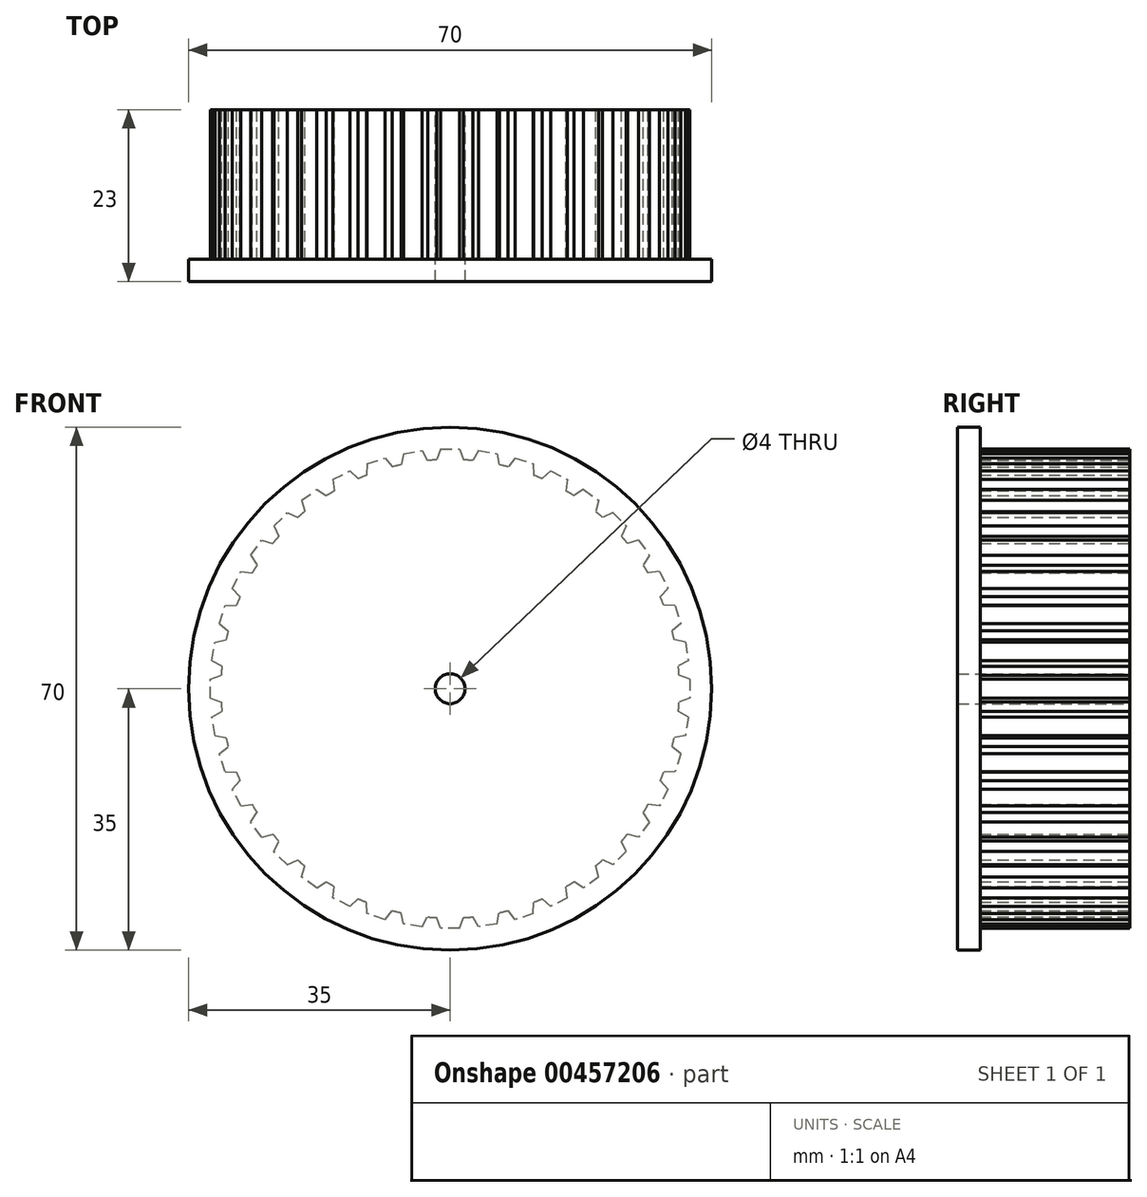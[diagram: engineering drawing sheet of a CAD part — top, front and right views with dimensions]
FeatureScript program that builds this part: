
annotation { "Feature Type Name" : "Feature", "Feature Type Description" : "" }
export const myFeature = defineFeature(function(context is Context, id is Id, definition is map)
    precondition{}
    {
        {
            var Q0;
            Q0=qCreatedBy(makeId("Front.planeOp"),FACE);
            var sketch = newSketch(context, id + "F0", { "sketchPlane" : qUnion([Q0])});
            skCircle(sketch, "E0", {"center": v(0, 0) * mm, "radius": 32.09 * mm, "construction": true});
            skLineSegment(sketch, "E1", {"start": v(0, 32.09) * mm, "end": v(0, 30.69) * mm, "construction": true});
            skCircle(sketch, "E2", {"center": v(0, 0) * mm, "radius": 30.69 * mm});
            skLineSegment(sketch, "E3", {"start": v(0, 0) * mm, "end": v(-1.26, 32.06) * mm, "construction": true});
            skLineSegment(sketch, "E4", {"start": v(0, 0) * mm, "end": v(-2.52, 31.99) * mm, "construction": true});
            skLineSegment(sketch, "E5.MirrorCS", {"start": v(0, 0) * mm, "end": v(1.26, 32.06) * mm, "construction": true});
            skLineSegment(sketch, "E6.MirrorCS", {"start": v(0, 0) * mm, "end": v(2.52, 31.99) * mm, "construction": true});
            skLineSegment(sketch, "E7", {"start": v(-1.26, 32.06) * mm, "end": v(1.26, 32.06) * mm});
            skLineSegment(sketch, "E8", {"start": v(-1.26, 32.06) * mm, "end": v(-1.8, 30.63) * mm});
            skLineSegment(sketch, "E9.MirrorCS", {"start": v(1.26, 32.06) * mm, "end": v(1.8, 30.63) * mm});
            skLineSegment(sketch, "E10.1.0", {"start": v(-6.26, 31.47) * mm, "end": v(-6.56, 29.97) * mm});
            skLineSegment(sketch, "E10.1.1", {"start": v(-6.26, 31.47) * mm, "end": v(-3.77, 31.86) * mm});
            skLineSegment(sketch, "E10.1.2", {"start": v(-3.77, 31.86) * mm, "end": v(-3.02, 30.54) * mm});
            skLineSegment(sketch, "E10.2.0", {"start": v(-11.1, 30.1) * mm, "end": v(-11.17, 28.58) * mm});
            skLineSegment(sketch, "E10.2.1", {"start": v(-11.1, 30.1) * mm, "end": v(-8.7, 30.88) * mm});
            skLineSegment(sketch, "E10.2.2", {"start": v(-8.7, 30.88) * mm, "end": v(-7.76, 29.69) * mm});
            skLineSegment(sketch, "E10.3.0", {"start": v(-15.68, 28) * mm, "end": v(-15.5, 26.48) * mm});
            skLineSegment(sketch, "E10.3.1", {"start": v(-15.68, 28) * mm, "end": v(-13.43, 29.14) * mm});
            skLineSegment(sketch, "E10.3.2", {"start": v(-13.43, 29.14) * mm, "end": v(-12.3, 28.1) * mm});
            skLineSegment(sketch, "E10.4.0", {"start": v(-19.86, 25.2) * mm, "end": v(-19.46, 23.73) * mm});
            skLineSegment(sketch, "E10.4.1", {"start": v(-19.86, 25.2) * mm, "end": v(-17.83, 26.68) * mm});
            skLineSegment(sketch, "E10.4.2", {"start": v(-17.83, 26.68) * mm, "end": v(-16.55, 25.84) * mm});
            skLineSegment(sketch, "E10.5.0", {"start": v(-23.56, 21.78) * mm, "end": v(-22.93, 20.4) * mm});
            skLineSegment(sketch, "E10.5.1", {"start": v(-23.56, 21.78) * mm, "end": v(-21.78, 23.56) * mm});
            skLineSegment(sketch, "E10.5.2", {"start": v(-21.78, 23.56) * mm, "end": v(-20.4, 22.93) * mm});
            skLineSegment(sketch, "E10.6.0", {"start": v(-26.68, 17.83) * mm, "end": v(-25.84, 16.55) * mm});
            skLineSegment(sketch, "E10.6.1", {"start": v(-26.68, 17.83) * mm, "end": v(-25.2, 19.86) * mm});
            skLineSegment(sketch, "E10.6.2", {"start": v(-25.2, 19.86) * mm, "end": v(-23.73, 19.46) * mm});
            skLineSegment(sketch, "E10.7.0", {"start": v(-29.14, 13.43) * mm, "end": v(-28.1, 12.3) * mm});
            skLineSegment(sketch, "E10.7.1", {"start": v(-29.14, 13.43) * mm, "end": v(-28, 15.68) * mm});
            skLineSegment(sketch, "E10.7.2", {"start": v(-28, 15.68) * mm, "end": v(-26.48, 15.5) * mm});
            skLineSegment(sketch, "E10.8.0", {"start": v(-30.88, 8.7) * mm, "end": v(-29.69, 7.76) * mm});
            skLineSegment(sketch, "E10.8.1", {"start": v(-30.88, 8.7) * mm, "end": v(-30.1, 11.1) * mm});
            skLineSegment(sketch, "E10.8.2", {"start": v(-30.1, 11.1) * mm, "end": v(-28.58, 11.17) * mm});
            skLineSegment(sketch, "E10.9.0", {"start": v(-31.86, 3.77) * mm, "end": v(-30.54, 3.02) * mm});
            skLineSegment(sketch, "E10.9.1", {"start": v(-31.86, 3.77) * mm, "end": v(-31.47, 6.26) * mm});
            skLineSegment(sketch, "E10.9.2", {"start": v(-31.47, 6.26) * mm, "end": v(-29.97, 6.56) * mm});
            skLineSegment(sketch, "E11", {"start": v(0, 0) * mm, "end": v(0, 32.09) * mm, "construction": true});
            skLineSegment(sketch, "E12.2.10.0", {"start": v(-32.06, -1.26) * mm, "end": v(-30.63, -1.8) * mm});
            skLineSegment(sketch, "E12.3.10.0", {"start": v(-32.06, -1.26) * mm, "end": v(-32.06, 1.26) * mm});
            skLineSegment(sketch, "E12.6.10.0", {"start": v(-32.06, 1.26) * mm, "end": v(-30.63, 1.8) * mm});
            skLineSegment(sketch, "E12.2.11.0", {"start": v(-31.47, -6.26) * mm, "end": v(-29.97, -6.56) * mm});
            skLineSegment(sketch, "E12.3.11.0", {"start": v(-31.47, -6.26) * mm, "end": v(-31.86, -3.77) * mm});
            skLineSegment(sketch, "E12.6.11.0", {"start": v(-31.86, -3.77) * mm, "end": v(-30.54, -3.02) * mm});
            skLineSegment(sketch, "E12.2.12.0", {"start": v(-30.1, -11.1) * mm, "end": v(-28.58, -11.17) * mm});
            skLineSegment(sketch, "E12.3.12.0", {"start": v(-30.1, -11.1) * mm, "end": v(-30.88, -8.7) * mm});
            skLineSegment(sketch, "E12.6.12.0", {"start": v(-30.88, -8.7) * mm, "end": v(-29.69, -7.76) * mm});
            skLineSegment(sketch, "E12.2.13.0", {"start": v(-28, -15.68) * mm, "end": v(-26.48, -15.5) * mm});
            skLineSegment(sketch, "E12.3.13.0", {"start": v(-28, -15.68) * mm, "end": v(-29.14, -13.43) * mm});
            skLineSegment(sketch, "E12.6.13.0", {"start": v(-29.14, -13.43) * mm, "end": v(-28.1, -12.3) * mm});
            skLineSegment(sketch, "E12.2.14.0", {"start": v(-25.2, -19.86) * mm, "end": v(-23.73, -19.46) * mm});
            skLineSegment(sketch, "E12.3.14.0", {"start": v(-25.2, -19.86) * mm, "end": v(-26.68, -17.83) * mm});
            skLineSegment(sketch, "E12.6.14.0", {"start": v(-26.68, -17.83) * mm, "end": v(-25.84, -16.55) * mm});
            skLineSegment(sketch, "E12.2.15.0", {"start": v(-21.78, -23.56) * mm, "end": v(-20.4, -22.93) * mm});
            skLineSegment(sketch, "E12.3.15.0", {"start": v(-21.78, -23.56) * mm, "end": v(-23.56, -21.78) * mm});
            skLineSegment(sketch, "E12.6.15.0", {"start": v(-23.56, -21.78) * mm, "end": v(-22.93, -20.4) * mm});
            skLineSegment(sketch, "E12.2.16.0", {"start": v(-17.83, -26.68) * mm, "end": v(-16.55, -25.84) * mm});
            skLineSegment(sketch, "E12.3.16.0", {"start": v(-17.83, -26.68) * mm, "end": v(-19.86, -25.2) * mm});
            skLineSegment(sketch, "E12.6.16.0", {"start": v(-19.86, -25.2) * mm, "end": v(-19.46, -23.73) * mm});
            skLineSegment(sketch, "E12.2.17.0", {"start": v(-13.43, -29.14) * mm, "end": v(-12.3, -28.1) * mm});
            skLineSegment(sketch, "E12.3.17.0", {"start": v(-13.43, -29.14) * mm, "end": v(-15.68, -28) * mm});
            skLineSegment(sketch, "E12.6.17.0", {"start": v(-15.68, -28) * mm, "end": v(-15.5, -26.48) * mm});
            skLineSegment(sketch, "E12.2.18.0", {"start": v(-8.7, -30.88) * mm, "end": v(-7.76, -29.69) * mm});
            skLineSegment(sketch, "E12.3.18.0", {"start": v(-8.7, -30.88) * mm, "end": v(-11.1, -30.1) * mm});
            skLineSegment(sketch, "E12.6.18.0", {"start": v(-11.1, -30.1) * mm, "end": v(-11.17, -28.58) * mm});
            skLineSegment(sketch, "E12.2.19.0", {"start": v(-3.77, -31.86) * mm, "end": v(-3.02, -30.54) * mm});
            skLineSegment(sketch, "E12.3.19.0", {"start": v(-3.77, -31.86) * mm, "end": v(-6.26, -31.47) * mm});
            skLineSegment(sketch, "E12.6.19.0", {"start": v(-6.26, -31.47) * mm, "end": v(-6.56, -29.97) * mm});
            skLineSegment(sketch, "E12.2.20.0", {"start": v(1.26, -32.06) * mm, "end": v(1.8, -30.63) * mm});
            skLineSegment(sketch, "E12.3.20.0", {"start": v(1.26, -32.06) * mm, "end": v(-1.26, -32.06) * mm});
            skLineSegment(sketch, "E12.6.20.0", {"start": v(-1.26, -32.06) * mm, "end": v(-1.8, -30.63) * mm});
            skLineSegment(sketch, "E12.2.21.0", {"start": v(6.26, -31.47) * mm, "end": v(6.56, -29.97) * mm});
            skLineSegment(sketch, "E12.3.21.0", {"start": v(6.26, -31.47) * mm, "end": v(3.77, -31.86) * mm});
            skLineSegment(sketch, "E12.6.21.0", {"start": v(3.77, -31.86) * mm, "end": v(3.02, -30.54) * mm});
            skLineSegment(sketch, "E12.2.22.0", {"start": v(11.1, -30.1) * mm, "end": v(11.17, -28.58) * mm});
            skLineSegment(sketch, "E12.3.22.0", {"start": v(11.1, -30.1) * mm, "end": v(8.7, -30.88) * mm});
            skLineSegment(sketch, "E12.6.22.0", {"start": v(8.7, -30.88) * mm, "end": v(7.76, -29.69) * mm});
            skLineSegment(sketch, "E12.2.23.0", {"start": v(15.68, -28) * mm, "end": v(15.5, -26.48) * mm});
            skLineSegment(sketch, "E12.3.23.0", {"start": v(15.68, -28) * mm, "end": v(13.43, -29.14) * mm});
            skLineSegment(sketch, "E12.6.23.0", {"start": v(13.43, -29.14) * mm, "end": v(12.3, -28.1) * mm});
            skLineSegment(sketch, "E12.2.24.0", {"start": v(19.86, -25.2) * mm, "end": v(19.46, -23.73) * mm});
            skLineSegment(sketch, "E12.3.24.0", {"start": v(19.86, -25.2) * mm, "end": v(17.83, -26.68) * mm});
            skLineSegment(sketch, "E12.6.24.0", {"start": v(17.83, -26.68) * mm, "end": v(16.55, -25.84) * mm});
            skLineSegment(sketch, "E12.2.25.0", {"start": v(23.56, -21.78) * mm, "end": v(22.93, -20.4) * mm});
            skLineSegment(sketch, "E12.3.25.0", {"start": v(23.56, -21.78) * mm, "end": v(21.78, -23.56) * mm});
            skLineSegment(sketch, "E12.6.25.0", {"start": v(21.78, -23.56) * mm, "end": v(20.4, -22.93) * mm});
            skLineSegment(sketch, "E12.2.26.0", {"start": v(26.68, -17.83) * mm, "end": v(25.84, -16.55) * mm});
            skLineSegment(sketch, "E12.3.26.0", {"start": v(26.68, -17.83) * mm, "end": v(25.2, -19.86) * mm});
            skLineSegment(sketch, "E12.6.26.0", {"start": v(25.2, -19.86) * mm, "end": v(23.73, -19.46) * mm});
            skLineSegment(sketch, "E12.2.27.0", {"start": v(29.14, -13.43) * mm, "end": v(28.1, -12.3) * mm});
            skLineSegment(sketch, "E12.3.27.0", {"start": v(29.14, -13.43) * mm, "end": v(28, -15.68) * mm});
            skLineSegment(sketch, "E12.6.27.0", {"start": v(28, -15.68) * mm, "end": v(26.48, -15.5) * mm});
            skLineSegment(sketch, "E12.2.28.0", {"start": v(30.88, -8.7) * mm, "end": v(29.69, -7.76) * mm});
            skLineSegment(sketch, "E12.3.28.0", {"start": v(30.88, -8.7) * mm, "end": v(30.1, -11.1) * mm});
            skLineSegment(sketch, "E12.6.28.0", {"start": v(30.1, -11.1) * mm, "end": v(28.58, -11.17) * mm});
            skLineSegment(sketch, "E12.2.29.0", {"start": v(31.86, -3.77) * mm, "end": v(30.54, -3.02) * mm});
            skLineSegment(sketch, "E12.3.29.0", {"start": v(31.86, -3.77) * mm, "end": v(31.47, -6.26) * mm});
            skLineSegment(sketch, "E12.6.29.0", {"start": v(31.47, -6.26) * mm, "end": v(29.97, -6.56) * mm});
            skLineSegment(sketch, "E12.2.30.0", {"start": v(32.06, 1.26) * mm, "end": v(30.63, 1.8) * mm});
            skLineSegment(sketch, "E12.3.30.0", {"start": v(32.06, 1.26) * mm, "end": v(32.06, -1.26) * mm});
            skLineSegment(sketch, "E12.6.30.0", {"start": v(32.06, -1.26) * mm, "end": v(30.63, -1.8) * mm});
            skLineSegment(sketch, "E12.2.31.0", {"start": v(31.47, 6.26) * mm, "end": v(29.97, 6.56) * mm});
            skLineSegment(sketch, "E12.3.31.0", {"start": v(31.47, 6.26) * mm, "end": v(31.86, 3.77) * mm});
            skLineSegment(sketch, "E12.6.31.0", {"start": v(31.86, 3.77) * mm, "end": v(30.54, 3.02) * mm});
            skLineSegment(sketch, "E12.2.32.0", {"start": v(30.1, 11.1) * mm, "end": v(28.58, 11.17) * mm});
            skLineSegment(sketch, "E12.3.32.0", {"start": v(30.1, 11.1) * mm, "end": v(30.88, 8.7) * mm});
            skLineSegment(sketch, "E12.6.32.0", {"start": v(30.88, 8.7) * mm, "end": v(29.69, 7.76) * mm});
            skLineSegment(sketch, "E12.2.33.0", {"start": v(28, 15.68) * mm, "end": v(26.48, 15.5) * mm});
            skLineSegment(sketch, "E12.3.33.0", {"start": v(28, 15.68) * mm, "end": v(29.14, 13.43) * mm});
            skLineSegment(sketch, "E12.6.33.0", {"start": v(29.14, 13.43) * mm, "end": v(28.1, 12.3) * mm});
            skLineSegment(sketch, "E12.2.34.0", {"start": v(25.2, 19.86) * mm, "end": v(23.73, 19.46) * mm});
            skLineSegment(sketch, "E12.3.34.0", {"start": v(25.2, 19.86) * mm, "end": v(26.68, 17.83) * mm});
            skLineSegment(sketch, "E12.6.34.0", {"start": v(26.68, 17.83) * mm, "end": v(25.84, 16.55) * mm});
            skLineSegment(sketch, "E12.2.35.0", {"start": v(21.78, 23.56) * mm, "end": v(20.4, 22.93) * mm});
            skLineSegment(sketch, "E12.3.35.0", {"start": v(21.78, 23.56) * mm, "end": v(23.56, 21.78) * mm});
            skLineSegment(sketch, "E12.6.35.0", {"start": v(23.56, 21.78) * mm, "end": v(22.93, 20.4) * mm});
            skLineSegment(sketch, "E12.2.36.0", {"start": v(17.83, 26.68) * mm, "end": v(16.55, 25.84) * mm});
            skLineSegment(sketch, "E12.3.36.0", {"start": v(17.83, 26.68) * mm, "end": v(19.86, 25.2) * mm});
            skLineSegment(sketch, "E12.6.36.0", {"start": v(19.86, 25.2) * mm, "end": v(19.46, 23.73) * mm});
            skLineSegment(sketch, "E12.2.37.0", {"start": v(13.43, 29.14) * mm, "end": v(12.3, 28.1) * mm});
            skLineSegment(sketch, "E12.3.37.0", {"start": v(13.43, 29.14) * mm, "end": v(15.68, 28) * mm});
            skLineSegment(sketch, "E12.6.37.0", {"start": v(15.68, 28) * mm, "end": v(15.5, 26.48) * mm});
            skLineSegment(sketch, "E12.2.38.0", {"start": v(8.7, 30.88) * mm, "end": v(7.76, 29.69) * mm});
            skLineSegment(sketch, "E12.3.38.0", {"start": v(8.7, 30.88) * mm, "end": v(11.1, 30.1) * mm});
            skLineSegment(sketch, "E12.6.38.0", {"start": v(11.1, 30.1) * mm, "end": v(11.17, 28.58) * mm});
            skLineSegment(sketch, "E12.2.39.0", {"start": v(3.77, 31.86) * mm, "end": v(3.02, 30.54) * mm});
            skLineSegment(sketch, "E12.3.39.0", {"start": v(3.77, 31.86) * mm, "end": v(6.26, 31.47) * mm});
            skLineSegment(sketch, "E12.6.39.0", {"start": v(6.26, 31.47) * mm, "end": v(6.56, 29.97) * mm});
            skCircle(sketch, "E13", {"center": v(0, 0) * mm, "radius": 2 * mm});
            skSolve(sketch);
        }
        {
            var Q0;
            Q0=qSketchRegion(id+"F0",true);
            extrude(context, id + "F1", {"entities" : qUnion([Q0]), "depth" : 20 * mm, "offsetDistance" : 25 * mm});
        }
        {
            var Q0;
            Q0=makeQuery(id+"F1.opExtrude","CAP_FACE",FACE,{"disambiguationData":[OSD([sQuery(id+"F0.wireOp",EDGE,"E2"),sQuery(id+"F0.wireOp",EDGE,"E7"),sQuery(id+"F0.wireOp",EDGE,"E8"),sQuery(id+"F0.wireOp",EDGE,"E9.MirrorCS"),sQuery(id+"F0.wireOp",EDGE,"E10.1.0"),sQuery(id+"F0.wireOp",EDGE,"E10.1.1"),sQuery(id+"F0.wireOp",EDGE,"E10.1.2"),sQuery(id+"F0.wireOp",EDGE,"E10.2.0"),sQuery(id+"F0.wireOp",EDGE,"E10.2.1"),sQuery(id+"F0.wireOp",EDGE,"E10.2.2"),sQuery(id+"F0.wireOp",EDGE,"E10.3.0"),sQuery(id+"F0.wireOp",EDGE,"E10.3.1"),sQuery(id+"F0.wireOp",EDGE,"E10.3.2"),sQuery(id+"F0.wireOp",EDGE,"E10.4.0"),sQuery(id+"F0.wireOp",EDGE,"E10.4.1"),sQuery(id+"F0.wireOp",EDGE,"E10.4.2"),sQuery(id+"F0.wireOp",EDGE,"E10.5.0"),sQuery(id+"F0.wireOp",EDGE,"E10.5.1"),sQuery(id+"F0.wireOp",EDGE,"E10.5.2"),sQuery(id+"F0.wireOp",EDGE,"E10.6.0"),sQuery(id+"F0.wireOp",EDGE,"E10.6.1"),sQuery(id+"F0.wireOp",EDGE,"E10.6.2"),sQuery(id+"F0.wireOp",EDGE,"E10.7.0"),sQuery(id+"F0.wireOp",EDGE,"E10.7.1"),sQuery(id+"F0.wireOp",EDGE,"E10.7.2"),sQuery(id+"F0.wireOp",EDGE,"E10.8.0"),sQuery(id+"F0.wireOp",EDGE,"E10.8.1"),sQuery(id+"F0.wireOp",EDGE,"E10.8.2"),sQuery(id+"F0.wireOp",EDGE,"E10.9.0"),sQuery(id+"F0.wireOp",EDGE,"E10.9.1"),sQuery(id+"F0.wireOp",EDGE,"E10.9.2"),sQuery(id+"F0.wireOp",EDGE,"E12.2.10.0"),sQuery(id+"F0.wireOp",EDGE,"E12.3.10.0"),sQuery(id+"F0.wireOp",EDGE,"E12.6.10.0"),sQuery(id+"F0.wireOp",EDGE,"E12.2.11.0"),sQuery(id+"F0.wireOp",EDGE,"E12.3.11.0"),sQuery(id+"F0.wireOp",EDGE,"E12.6.11.0"),sQuery(id+"F0.wireOp",EDGE,"E12.2.12.0"),sQuery(id+"F0.wireOp",EDGE,"E12.3.12.0"),sQuery(id+"F0.wireOp",EDGE,"E12.6.12.0"),sQuery(id+"F0.wireOp",EDGE,"E12.2.13.0"),sQuery(id+"F0.wireOp",EDGE,"E12.3.13.0"),sQuery(id+"F0.wireOp",EDGE,"E12.6.13.0"),sQuery(id+"F0.wireOp",EDGE,"E12.2.14.0"),sQuery(id+"F0.wireOp",EDGE,"E12.3.14.0"),sQuery(id+"F0.wireOp",EDGE,"E12.6.14.0"),sQuery(id+"F0.wireOp",EDGE,"E12.2.15.0"),sQuery(id+"F0.wireOp",EDGE,"E12.3.15.0"),sQuery(id+"F0.wireOp",EDGE,"E12.6.15.0"),sQuery(id+"F0.wireOp",EDGE,"E12.2.16.0"),sQuery(id+"F0.wireOp",EDGE,"E12.3.16.0"),sQuery(id+"F0.wireOp",EDGE,"E12.6.16.0"),sQuery(id+"F0.wireOp",EDGE,"E12.2.17.0"),sQuery(id+"F0.wireOp",EDGE,"E12.3.17.0"),sQuery(id+"F0.wireOp",EDGE,"E12.6.17.0"),sQuery(id+"F0.wireOp",EDGE,"E12.2.18.0"),sQuery(id+"F0.wireOp",EDGE,"E12.3.18.0"),sQuery(id+"F0.wireOp",EDGE,"E12.6.18.0"),sQuery(id+"F0.wireOp",EDGE,"E12.2.19.0"),sQuery(id+"F0.wireOp",EDGE,"E12.3.19.0"),sQuery(id+"F0.wireOp",EDGE,"E12.6.19.0"),sQuery(id+"F0.wireOp",EDGE,"E12.2.20.0"),sQuery(id+"F0.wireOp",EDGE,"E12.3.20.0"),sQuery(id+"F0.wireOp",EDGE,"E12.6.20.0"),sQuery(id+"F0.wireOp",EDGE,"E12.2.21.0"),sQuery(id+"F0.wireOp",EDGE,"E12.3.21.0"),sQuery(id+"F0.wireOp",EDGE,"E12.6.21.0"),sQuery(id+"F0.wireOp",EDGE,"E12.2.22.0"),sQuery(id+"F0.wireOp",EDGE,"E12.3.22.0"),sQuery(id+"F0.wireOp",EDGE,"E12.6.22.0"),sQuery(id+"F0.wireOp",EDGE,"E12.2.23.0"),sQuery(id+"F0.wireOp",EDGE,"E12.3.23.0"),sQuery(id+"F0.wireOp",EDGE,"E12.6.23.0"),sQuery(id+"F0.wireOp",EDGE,"E12.2.24.0"),sQuery(id+"F0.wireOp",EDGE,"E12.3.24.0"),sQuery(id+"F0.wireOp",EDGE,"E12.6.24.0"),sQuery(id+"F0.wireOp",EDGE,"E12.2.25.0"),sQuery(id+"F0.wireOp",EDGE,"E12.3.25.0"),sQuery(id+"F0.wireOp",EDGE,"E12.6.25.0"),sQuery(id+"F0.wireOp",EDGE,"E12.2.26.0"),sQuery(id+"F0.wireOp",EDGE,"E12.3.26.0"),sQuery(id+"F0.wireOp",EDGE,"E12.6.26.0"),sQuery(id+"F0.wireOp",EDGE,"E12.2.27.0"),sQuery(id+"F0.wireOp",EDGE,"E12.3.27.0"),sQuery(id+"F0.wireOp",EDGE,"E12.6.27.0"),sQuery(id+"F0.wireOp",EDGE,"E12.2.28.0"),sQuery(id+"F0.wireOp",EDGE,"E12.3.28.0"),sQuery(id+"F0.wireOp",EDGE,"E12.6.28.0"),sQuery(id+"F0.wireOp",EDGE,"E12.2.29.0"),sQuery(id+"F0.wireOp",EDGE,"E12.3.29.0"),sQuery(id+"F0.wireOp",EDGE,"E12.6.29.0"),sQuery(id+"F0.wireOp",EDGE,"E12.2.30.0"),sQuery(id+"F0.wireOp",EDGE,"E12.3.30.0"),sQuery(id+"F0.wireOp",EDGE,"E12.6.30.0"),sQuery(id+"F0.wireOp",EDGE,"E12.2.31.0"),sQuery(id+"F0.wireOp",EDGE,"E12.3.31.0"),sQuery(id+"F0.wireOp",EDGE,"E12.6.31.0"),sQuery(id+"F0.wireOp",EDGE,"E12.2.32.0"),sQuery(id+"F0.wireOp",EDGE,"E12.3.32.0"),sQuery(id+"F0.wireOp",EDGE,"E12.6.32.0"),sQuery(id+"F0.wireOp",EDGE,"E12.2.33.0"),sQuery(id+"F0.wireOp",EDGE,"E12.3.33.0"),sQuery(id+"F0.wireOp",EDGE,"E12.6.33.0"),sQuery(id+"F0.wireOp",EDGE,"E12.2.34.0"),sQuery(id+"F0.wireOp",EDGE,"E12.3.34.0"),sQuery(id+"F0.wireOp",EDGE,"E12.6.34.0"),sQuery(id+"F0.wireOp",EDGE,"E12.2.35.0"),sQuery(id+"F0.wireOp",EDGE,"E12.3.35.0"),sQuery(id+"F0.wireOp",EDGE,"E12.6.35.0"),sQuery(id+"F0.wireOp",EDGE,"E12.2.36.0"),sQuery(id+"F0.wireOp",EDGE,"E12.3.36.0"),sQuery(id+"F0.wireOp",EDGE,"E12.6.36.0"),sQuery(id+"F0.wireOp",EDGE,"E12.2.37.0"),sQuery(id+"F0.wireOp",EDGE,"E12.3.37.0"),sQuery(id+"F0.wireOp",EDGE,"E12.6.37.0"),sQuery(id+"F0.wireOp",EDGE,"E12.2.38.0"),sQuery(id+"F0.wireOp",EDGE,"E12.3.38.0"),sQuery(id+"F0.wireOp",EDGE,"E12.6.38.0"),sQuery(id+"F0.wireOp",EDGE,"E12.2.39.0"),sQuery(id+"F0.wireOp",EDGE,"E12.3.39.0"),sQuery(id+"F0.wireOp",EDGE,"E12.6.39.0"),sQuery(id+"F0.wireOp",EDGE,"E13")])],"isStart":false});
            var sketch = newSketch(context, id + "F2", { "sketchPlane" : qUnion([Q0])});
            skCircle(sketch, "E14", {"center": v(0, 0) * mm, "radius": 35 * mm});
            skCircle(sketch, "E15", {"center": v(0, 0) * mm, "radius": 2 * mm});
            skSolve(sketch);
        }
        {
            var Q0;
            Q0 = qSketchRegion(id + "F2", true);
            extrude(context, id + "F3", {"entities" : qUnion([Q0]), "operationType" : NewBodyOperationType.ADD, "depth" : 3 * mm, "offsetDistance" : 25 * mm});
        }
    });
